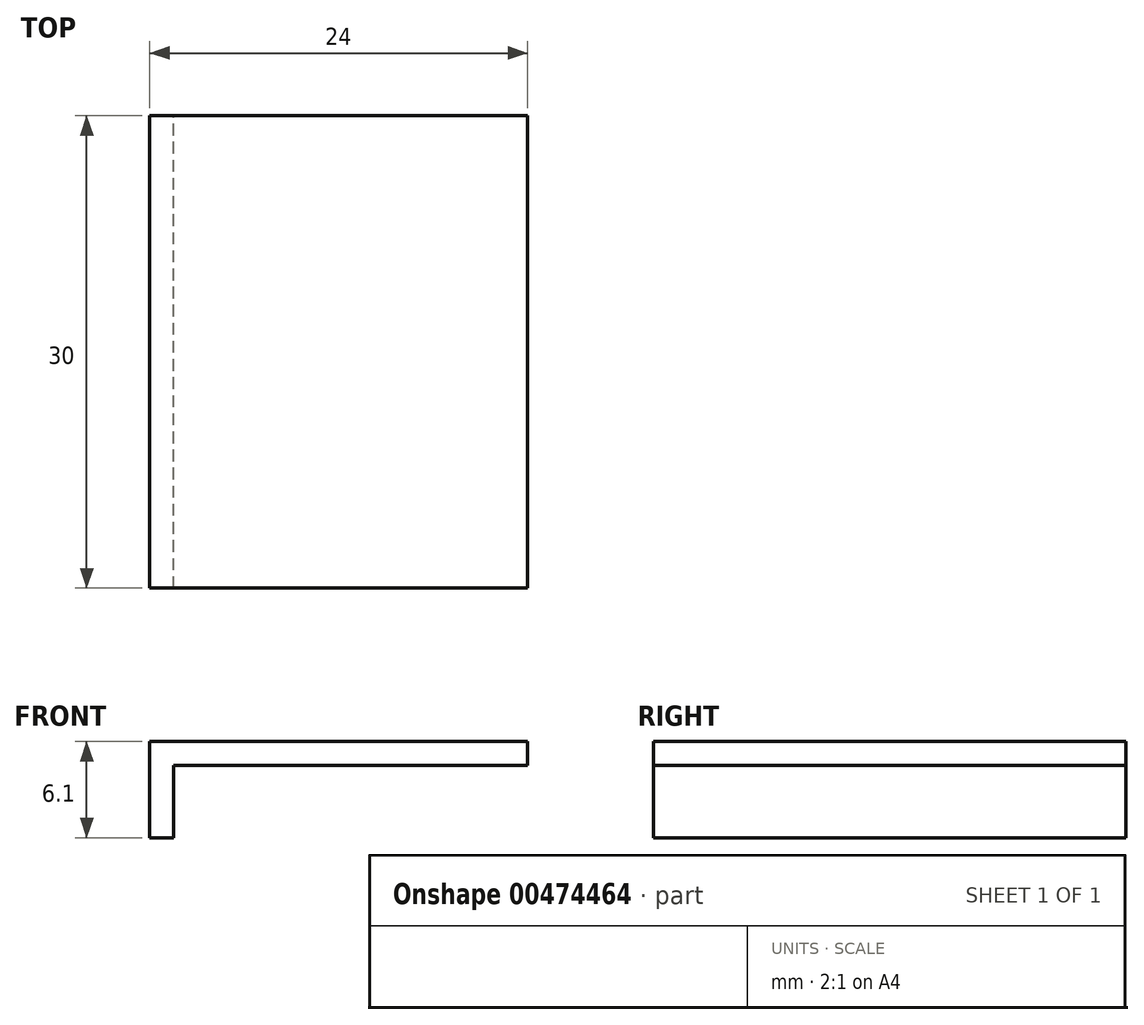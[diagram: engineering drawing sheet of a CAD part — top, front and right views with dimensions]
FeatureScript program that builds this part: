
annotation { "Feature Type Name" : "Feature", "Feature Type Description" : "" }
export const myFeature = defineFeature(function(context is Context, id is Id, definition is map)
    precondition{}
    {
        {
            var Q0;
            Q0=qCreatedBy(makeId("Front.planeOp"),FACE);
            var sketch = newSketch(context, id + "F0", { "sketchPlane" : qUnion([Q0])});
            skLineSegment(sketch, "E0", {"start": v(-3.6, 0) * mm, "end": v(-5.1, 0) * mm});
            skLineSegment(sketch, "E1", {"start": v(-5.1, 0) * mm, "end": v(-5.1, 6.1) * mm});
            skLineSegment(sketch, "E2", {"start": v(-5.1, 6.1) * mm, "end": v(18.9, 6.1) * mm});
            skLineSegment(sketch, "E3", {"start": v(18.9, 6.1) * mm, "end": v(18.9, 4.6) * mm});
            skLineSegment(sketch, "E4", {"start": v(18.9, 4.6) * mm, "end": v(-3.6, 4.6) * mm});
            skLineSegment(sketch, "E5", {"start": v(-3.6, 4.6) * mm, "end": v(-3.6, 0) * mm});
            skSolve(sketch);
        }
        {
            var Q0;
            Q0=makeQuery(id+"F0.imprint","IMPRINT",FACE,{"disambiguationData":[TD([[makeQuery(id+"F0.imprint","IMPRINT",EDGE,{"derivedFrom":sQuery(id+"F0.wireOp",EDGE,"E0")}),-1.0]])]});
            extrude(context, id + "F1", {"entities" : qUnion([Q0]), "depth" : 30 * mm});
        }
    });
